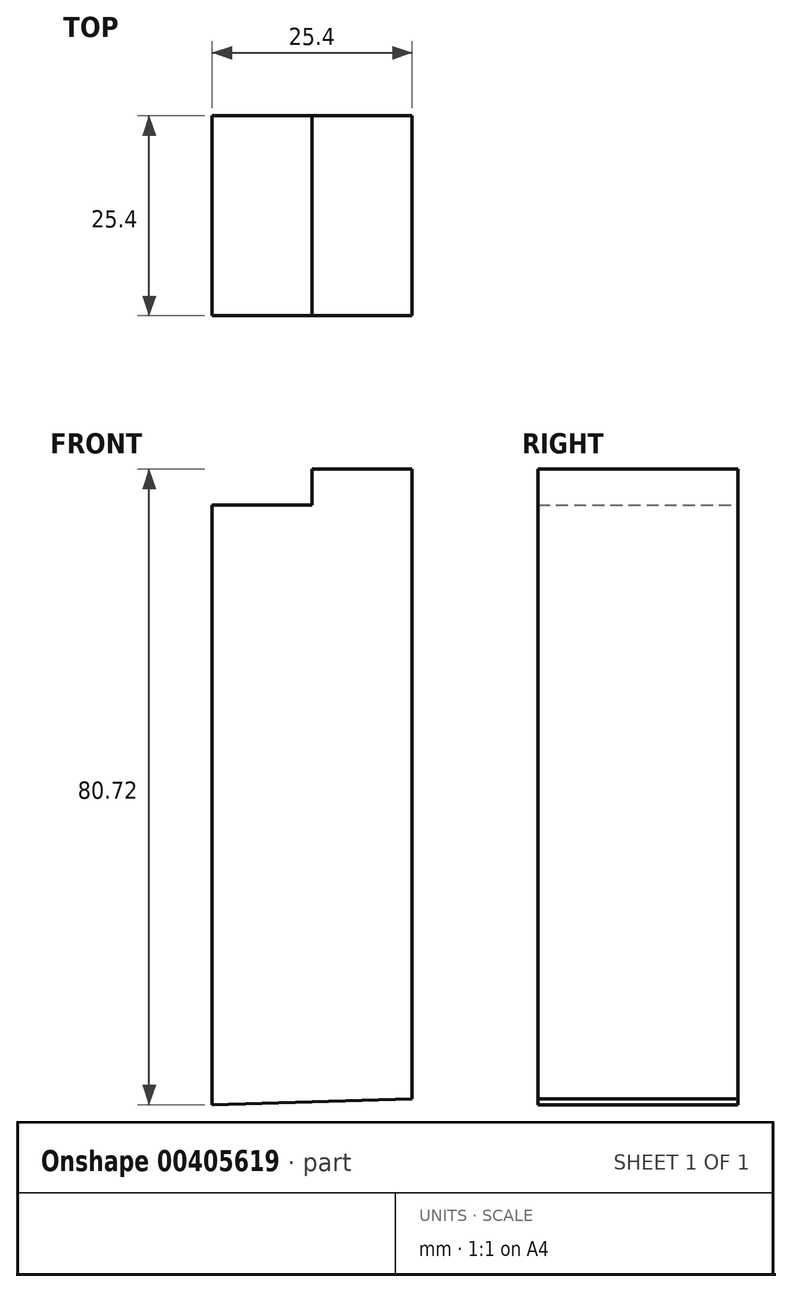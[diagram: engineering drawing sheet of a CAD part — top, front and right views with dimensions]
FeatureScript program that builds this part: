
annotation { "Feature Type Name" : "Feature", "Feature Type Description" : "" }
export const myFeature = defineFeature(function(context is Context, id is Id, definition is map)
    precondition{}
    {
        {
            var Q0;
            Q0=qCreatedBy(makeId("Front.planeOp"),FACE);
            var sketch = newSketch(context, id + "F0", { "sketchPlane" : qUnion([Q0])});
            skLineSegment(sketch, "E0", {"start": v(-31.94, -41.97) * mm, "end": v(-31.94, 34.23) * mm});
            skLineSegment(sketch, "E1", {"start": v(-31.94, 34.23) * mm, "end": v(-19.24, 34.23) * mm});
            skLineSegment(sketch, "E2", {"start": v(-19.24, 34.23) * mm, "end": v(-19.24, 38.75) * mm});
            skLineSegment(sketch, "E3", {"start": v(-19.24, 38.75) * mm, "end": v(-6.54, 38.75) * mm});
            skLineSegment(sketch, "E4", {"start": v(-6.54, 38.75) * mm, "end": v(-6.54, -41.26) * mm});
            skLineSegment(sketch, "E5", {"start": v(-6.54, -41.26) * mm, "end": v(-31.94, -41.97) * mm});
            skSolve(sketch);
        }
        {
            var Q0;
            Q0 = qSketchRegion(id + "F0", true);
            extrude(context, id + "F1", {"entities" : qUnion([Q0]), "endBound" : BoundingType.SYMMETRIC, "depth" : 25.4 * mm});
        }
        {
            var Q0;
            Q0=makeQuery(id+"F1.opExtrude","CAP_FACE",FACE,{"disambiguationData":[OSD([sQuery(id+"F0.wireOp",EDGE,"E0"),sQuery(id+"F0.wireOp",EDGE,"E1"),sQuery(id+"F0.wireOp",EDGE,"E2"),sQuery(id+"F0.wireOp",EDGE,"E3"),sQuery(id+"F0.wireOp",EDGE,"E4"),sQuery(id+"F0.wireOp",EDGE,"E5")])],"isStart":false});
            var sketch = newSketch(context, id + "F2", { "sketchPlane" : qUnion([Q0])});
            skSolve(sketch);
        }
        {
            var Q0;
            Q0=makeQuery(id+"F2.imprint","IMPRINT",FACE,{"disambiguationData":[TD([[makeQuery(id+"F2.imprint","IMPRINT",EDGE,{"derivedFrom":makeQuery(id+"F1.opExtrude","CAP_EDGE",EDGE,{"disambiguationData":[OSD([sQuery(id+"F0.wireOp",EDGE,"E0")])],"isStart":false})}),-1.0]])]});
            var sketch = newSketch(context, id + "F3", { "sketchPlane" : qUnion([Q0])});
            skCircle(sketch, "E6", {"center": v(-18.24, 17.95) * mm, "radius": 3.81 * mm});
            skCircle(sketch, "E7", {"center": v(-18.5, 5.9) * mm, "radius": 3.81 * mm});
            skCircle(sketch, "E8", {"center": v(-17.98, -9.73) * mm, "radius": 3.81 * mm});
            skCircle(sketch, "E9", {"center": v(-16.44, -32.28) * mm, "radius": 3.81 * mm});
            skCircle(sketch, "E10", {"center": v(-18.5, -20.24) * mm, "radius": 3.81 * mm});
            skCircle(sketch, "E11", {"center": v(-18.5, 29.23) * mm, "radius": 3.81 * mm});
            skSolve(sketch);
        }
        {
            var Q0;
            Q0=sQuery(id+"F3.wireOp",EDGE,"E11");
            extrude(context, id + "F4", {"bodyType" : ToolBodyType.SURFACE, "operationType" : NewBodyOperationType.REMOVE, "surfaceEntities" : qUnion([Q0]), "endBound" : BoundingType.UP_TO_NEXT, "oppositeDirection" : true, "depth" : 25.4 * mm});
        }
    });
